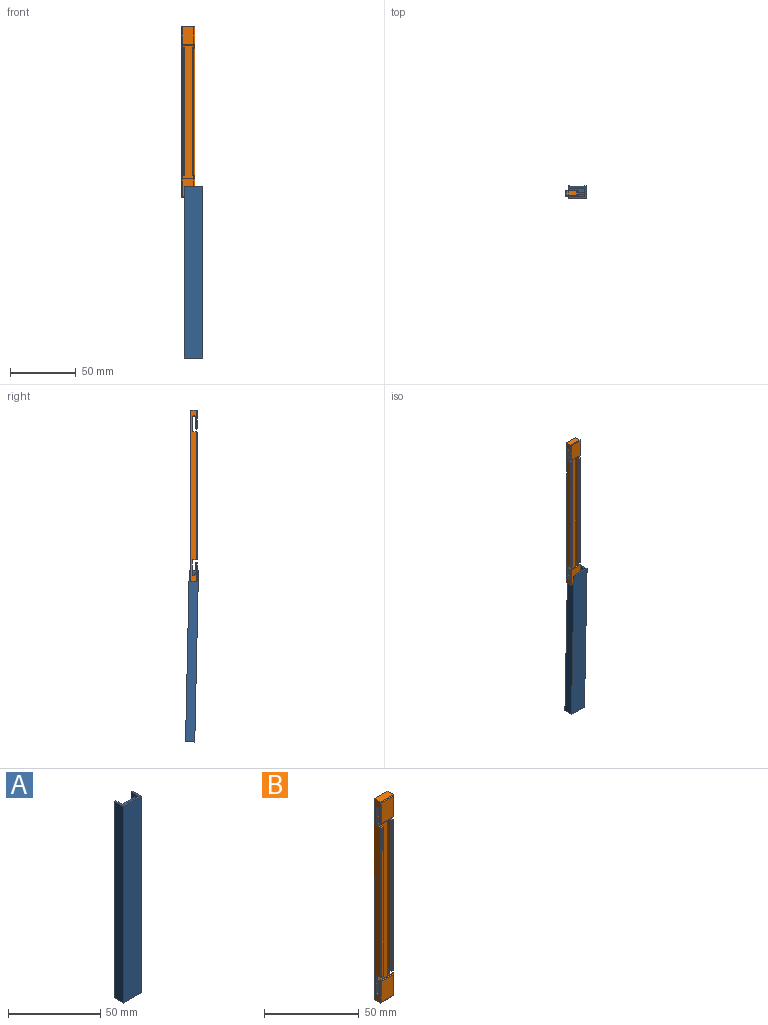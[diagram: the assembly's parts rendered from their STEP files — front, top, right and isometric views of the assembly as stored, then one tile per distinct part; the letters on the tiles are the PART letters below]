
ASSEMBLY  parts=2 mates=1
PART A: 16 faces, bbox 14x7x130 mm
  f0: plane 130x7mm, normal (-1,0,0), area 910mm2, adj f1,f3,f4,f10
  f1: plane 130x14mm, normal (0,-1,0), area 1820mm2, adj f0,f2,f4,f10
  f2: plane 130x7mm, normal (1,0,0), area 910mm2, adj f1,f3,f4,f10
  f3: plane 130x14mm, normal (0,1,0), area 1237.4mm2, adj f0,f2,f4,f5,f7,f8,f10,f11
  f4: plane 14x7mm, normal (0,0,-1), area 28.4mm2, adj f0,f1,f2,f3,f5,f6,f7
  f5: plane 25x5.97mm, normal (1,0,0), area 146.8mm2, adj f3,f4,f6,f8,f9
  f6: plane 25x11.65mm, normal (0,1,0), area 291.3mm2, adj f4,f5,f7,f8
  f7: plane 25x5.97mm, normal (-1,0,0), area 146.8mm2, adj f3,f4,f6,f8,f9
  f8: plane 11.65x5.97mm, normal (0,0,-1), area 69.6mm2, adj f3,f5,f6,f7
  f9: cylinder r=0.9mm len=11.65mm, axis (1,0,0), area 65.9mm2, adj f5,f7
  f10: plane 14x7mm, normal (0,0,1), area 28.4mm2, adj f0,f1,f2,f3,f11,f12,f13
  f11: plane 25x5.97mm, normal (1,0,0), area 146.8mm2, adj f3,f10,f12,f14,f15
  f12: plane 25x11.65mm, normal (0,1,0), area 291.3mm2, adj f10,f11,f13,f14
  f13: plane 25x5.97mm, normal (-1,0,0), area 146.8mm2, adj f3,f10,f12,f14,f15
  f14: plane 11.65x5.97mm, normal (0,0,1), area 69.6mm2, adj f3,f11,f12,f13
  f15: cylinder r=0.9mm len=11.65mm, axis (1,0,0), area 65.9mm2, adj f11,f13
PART B: 66 faces, bbox 10x5x130 mm
  f0: plane 97.15x0.5mm, normal (-1,0,0), area 48.6mm2, adj f7,f12,f26,f51
  f1: plane 97.15x0.5mm, normal (1,0,0), area 48.6mm2, adj f6,f14,f27,f52
  f2: plane 96.15x1.09mm, normal (0,-1,0), area 105mm2, adj f14,f15,f40,f65
  f3: plane 96.15x0.91mm, normal (0,-1,0), area 87.3mm2, adj f12,f13,f39,f64
  f4: plane 130x4.5mm, normal (-1,0,0), area 533.9mm2, adj f8,f15,f17,f27,f28,f29,f30,f32
  f5: plane 130x4.5mm, normal (1,0,0), area 533.9mm2, adj f8,f13,f17,f24,f25,f26,f30,f31
  f6: plane 97.15x1.09mm, normal (0,1,0), area 106.1mm2, adj f1,f10,f27,f52
  f7: plane 97.15x0.91mm, normal (0,1,0), area 88.2mm2, adj f0,f11,f26,f51
  f8: plane 130x10mm, normal (0,1,0), area 1300mm2, adj f4,f5,f17,f42
  f9: plane 128x8mm, normal (0,-1,0), area 1012mm2, adj f10,f11,f18,f20,f21,f22,f23,f43
  f10: plane 128x3mm, normal (1,0,0), area 334.9mm2, adj f6,f9,f19,f20,f27,f28,f29,f30
  f11: plane 128x3mm, normal (-1,0,0), area 334.9mm2, adj f7,f9,f19,f23,f24,f25,f26,f30
  f12: cylinder r=0.5mm len=97.15mm, axis (0,0,1), area 76mm2, adj f0,f3,f39,f64
  f13: cylinder r=0.5mm len=97.15mm, axis (0,0,1), area 76mm2, adj f3,f5,f39,f64
  f14: cylinder r=0.5mm len=97.15mm, axis (0,0,-1), area 76mm2, adj f1,f2,f40,f65
  f15: cylinder r=0.5mm len=97.15mm, axis (0,0,-1), area 76mm2, adj f2,f4,f40,f65
  f16: plane 13.42x9mm, normal (0,-1,0), area 120.8mm2, adj f35,f36,f37,f38
  f17: plane 10x4.5mm, normal (0,0,-1), area 45mm2, adj f4,f5,f8,f37
  f18: plane 6x3mm, normal (0,0,1), area 18mm2, adj f9,f19,f21,f22
  f19: plane 13.29x8mm, normal (0,1,0), area 100.3mm2, adj f10,f11,f18,f20,f21,f22,f23,f30
  f20: plane 3x1.09mm, normal (0,0,1), area 3.3mm2, adj f9,f10,f19,f21
  f21: plane 3x1mm, normal (-1,0,0), area 3mm2, adj f9,f18,f19,f20
  f22: plane 3x1mm, normal (1,0,0), area 3mm2, adj f9,f18,f19,f23
  f23: plane 3x0.91mm, normal (0,0,1), area 2.7mm2, adj f9,f11,f19,f22
  f24: plane 8x1mm, normal (0,1,0), area 8mm2, adj f5,f11,f30,f31
  f25: plane 10x1mm, normal (0,-1,0), area 10mm2, adj f5,f11,f31,f34
  f26: plane 2x1.91mm, normal (0,0,-1), area 2.5mm2, adj f0,f5,f7,f11,f34,f39
  f27: plane 2.09x2mm, normal (0,0,-1), area 2.5mm2, adj f1,f4,f6,f10,f33,f40
  f28: plane 10x1mm, normal (0,-1,0), area 10mm2, adj f4,f10,f32,f33
  f29: plane 8x1mm, normal (0,1,0), area 8mm2, adj f4,f10,f30,f32
  f30: cylinder r=1mm len=10mm, axis (-1,0,0), area 7.3mm2, adj f4,f5,f10,f11,f19,f24,f29,f36
  f31: cylinder r=1mm len=2mm, axis (1,0,0), area 3.1mm2, adj f5,f11,f24,f25
  f32: cylinder r=1mm len=2mm, axis (1,0,0), area 3.1mm2, adj f4,f10,f28,f29
  f33: cylinder r=1mm len=1mm, axis (1,0,0), area 1.6mm2, adj f4,f10,f27,f28
  f34: cylinder r=1mm len=1mm, axis (1,0,0), area 1.6mm2, adj f5,f11,f25,f26
  f35: cylinder r=0.5mm len=14.42mm, axis (0,0,1), area 11mm2, adj f5,f16,f36,f37
  f36: cylinder r=0.5mm len=10mm, axis (-1,0,0), area 7.6mm2, adj f16,f30,f35,f38
  f37: cylinder r=0.5mm len=10mm, axis (1,0,0), area 7.6mm2, adj f16,f17,f35,f38
  f38: cylinder r=0.5mm len=14.42mm, axis (0,0,-1), area 11mm2, adj f4,f16,f36,f37
  f39: cylinder r=0.5mm len=1.91mm, axis (-1,0,0), area 1.2mm2, adj f3,f12,f13,f26
  f40: cylinder r=0.5mm len=2.09mm, axis (-1,0,0), area 1.4mm2, adj f2,f14,f15,f27
  f41: plane 13.42x9mm, normal (0,-1,0), area 120.8mm2, adj f60,f61,f62,f63
  f42: plane 10x4.5mm, normal (0,0,1), area 45mm2, adj f4,f5,f8,f62
  f43: plane 6x3mm, normal (0,0,-1), area 18mm2, adj f9,f44,f46,f47
  f44: plane 13.29x8mm, normal (0,1,0), area 100.3mm2, adj f10,f11,f43,f45,f46,f47,f48,f55
  f45: plane 3x1.09mm, normal (0,0,-1), area 3.3mm2, adj f9,f10,f44,f46
  f46: plane 3x1mm, normal (-1,0,0), area 3mm2, adj f9,f43,f44,f45
  f47: plane 3x1mm, normal (1,0,0), area 3mm2, adj f9,f43,f44,f48
  f48: plane 3x0.91mm, normal (0,0,-1), area 2.7mm2, adj f9,f11,f44,f47
  f49: plane 8x1mm, normal (0,1,0), area 8mm2, adj f5,f11,f55,f56
  f50: plane 10x1mm, normal (0,-1,0), area 10mm2, adj f5,f11,f56,f59
  f51: plane 2x1.91mm, normal (0,0,1), area 2.5mm2, adj f0,f5,f7,f11,f59,f64
  f52: plane 2.09x2mm, normal (0,0,1), area 2.5mm2, adj f1,f4,f6,f10,f58,f65
  f53: plane 10x1mm, normal (0,-1,0), area 10mm2, adj f4,f10,f57,f58
  f54: plane 8x1mm, normal (0,1,0), area 8mm2, adj f4,f10,f55,f57
  f55: cylinder r=1mm len=10mm, axis (-1,0,0), area 7.3mm2, adj f4,f5,f10,f11,f44,f49,f54,f61
  f56: cylinder r=1mm len=2mm, axis (1,0,0), area 3.1mm2, adj f5,f11,f49,f50
  f57: cylinder r=1mm len=2mm, axis (1,0,0), area 3.1mm2, adj f4,f10,f53,f54
  f58: cylinder r=1mm len=1mm, axis (1,0,0), area 1.6mm2, adj f4,f10,f52,f53
  f59: cylinder r=1mm len=1mm, axis (1,0,0), area 1.6mm2, adj f5,f11,f50,f51
  f60: cylinder r=0.5mm len=14.42mm, axis (0,0,-1), area 11mm2, adj f5,f41,f61,f62
  f61: cylinder r=0.5mm len=10mm, axis (-1,0,0), area 7.6mm2, adj f41,f55,f60,f63
  f62: cylinder r=0.5mm len=10mm, axis (1,0,0), area 7.6mm2, adj f41,f42,f60,f63
  f63: cylinder r=0.5mm len=14.42mm, axis (0,0,1), area 11mm2, adj f4,f41,f61,f62
  f64: cylinder r=0.5mm len=1.91mm, axis (-1,0,0), area 1.2mm2, adj f3,f12,f13,f51
  f65: cylinder r=0.5mm len=2.09mm, axis (-1,0,0), area 1.4mm2, adj f2,f14,f15,f52
PLACE A rot(axis=(1,0,0),1.2deg) t=(-25.17,-38.21,-49.28)mm
PLACE B t=(-5.56,-39.95,72.71)mm fixed
MATE revolute A.f15 <-> B.f31  axis (1,0,0) through (-11.46,-37.45,78.14)mm
